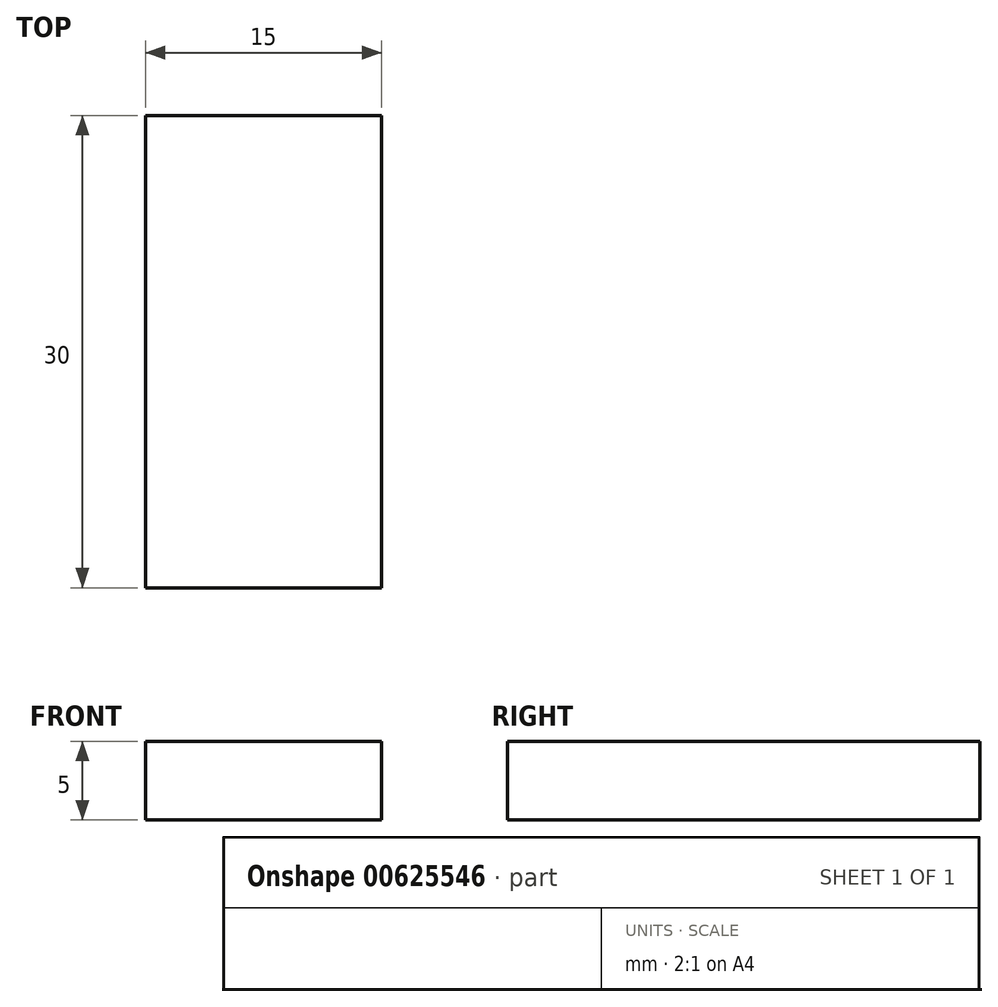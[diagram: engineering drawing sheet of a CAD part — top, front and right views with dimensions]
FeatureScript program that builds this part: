
annotation { "Feature Type Name" : "Feature", "Feature Type Description" : "" }
export const myFeature = defineFeature(function(context is Context, id is Id, definition is map)
    precondition{}
    {
        {
            var Q0;
            Q0=qCreatedBy(makeId("Top.planeOp"),FACE);
            var sketch = newSketch(context, id + "F0", { "sketchPlane" : qUnion([Q0])});
            skLineSegment(sketch, "E0.bottom", {"start": v(-7.5, 15) * mm, "end": v(7.5, 15) * mm});
            skLineSegment(sketch, "E0.top", {"start": v(-7.5, -15) * mm, "end": v(7.5, -15) * mm});
            skLineSegment(sketch, "E0.left", {"start": v(-7.5, 15) * mm, "end": v(-7.5, -15) * mm});
            skLineSegment(sketch, "E0.right", {"start": v(7.5, 15) * mm, "end": v(7.5, -15) * mm});
            skPoint(sketch, "E0.middle", {"position": v(0, 0) * mm});
            skSolve(sketch);
        }
        {
            var Q0;
            Q0 = qSketchRegion(id + "F0", true);
            extrude(context, id + "F1", {"entities" : qUnion([Q0]), "depth" : 5 * mm, "offsetDistance" : 25 * mm});
        }
    });
